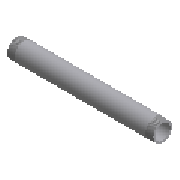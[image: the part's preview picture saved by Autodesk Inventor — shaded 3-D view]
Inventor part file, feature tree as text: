
AUTODESK INVENTOR PART (.ipt)
format: ipt  version: 2013 SP2 (Build 170200200, 200)  size: 157,696 bytes
history: native  units: mm (DEFAULTED — no unit token found)
features: other x6, sketch x3, revolve x1, plane x1, extrude x1
ambient origin geometry x8: Origin, YZ Plane, XZ Plane, XY Plane, X Axis, Y Axis, Z Axis, Center Point
bodies: Solid1 (feature_tree)
feature tree (12):
  revolve  "Revolution1"  [1 undecoded]
  other  "Work Axis1"
  other  "Work Point5"
  other  "Work Axis2"
  other  "Work Point6"
  other  "Work Axis3"
  other  "Work Axis4"
  plane  "Work Plane3"
  extrude  "Extrusion2"  Depth=130.6195mm
  sketch  "Sketch4"  dims[d28=90.0deg d4=17.34312mm d30=25.4mm d31=0.0mm d32=25.4mm d33=0.0mm d5=33.677098mm d39=50.8mm d40=50.8mm d41=0.0mm]
  sketch  "Sketch1"  dims[d0=33.401mm d1=0.312398mm]
  sketch  "Sketch3"  dims[d2=26.6446mm d3=130.6195mm]
note: 1 required parameter value undecoded (feature->parameter linkage not recoverable at this tier; creation-order binding heuristic only, values carry confidence <= 0.55)
